# Revit family: NORFAC_WENT2000_med lysning
name_source: partatom
category: Windows
revit_build: Autodesk Revit 2018 (Build: 20170525_2315(x64)
units: mm (PartAtom-declared; Revit-internal decimal feet)

## family parameters
Always vertical = Yes
Cut with Voids When Loaded = No
Host = Wall
OmniClass Number = 23.30.20.00
OmniClass Title = Windows
Room Calculation Point = No
Shared = No

## types (1)
- TS-1-1
    Analytic Construction = <None>
    Case/Transom = RAL 9010
    Default Sill Height = 800 mm
    Eref energi balance = 4.223619
    Ew nord = -44.319266
    Ew syd = 45.80705
    Ew vest = -9.139952
    Ew øst = -9.139952
    Frame Area = 0.43 m²
    Frame Depth = 140 mm  [stored 0.459318 ft]
    Frame Width = 92 mm
    Frame/Mullion = Softwood, Lumber
    Glass Area = 1.08 m²
    Glass Height = 1319 mm
    Glass Material = BA - (o) - Glas
    Glass Width = 816 mm
    Height = 1503 mm
    Horiz Mullion 1 of 1 = No
    Horiz Mullion 1 of 2 = No
    Horiz Mullion 2 of 2 = No
    Joint = 10 mm  [stored 0.0328084 ft]
    Joint Material = Black Rubber
    LT value = 0
    Left Hinging = Yes
    Lysning = <By Category>
    Manual Height = 1523 mm
    Manual Width = 1020 mm
    Placement In Wall = 0 mm  [stored 0 ft]
    Psi Glass = 0.04
    Right Hinging = No
    Rough Height = 1523 mm
    Rough Width = 1020 mm
    Top Hinging = No
    U value = 0.809317
    U value Frame = 0.71
    U value Glass = 0.69
    Ventil mål mm = 689.5
    Ventilations luftmængde 10Pa, m3/t = 23.6
    Ventilations luftsmængde 4Pa, m3/t = 14.9
    Ventilations luftsmængde 8Pa, m3/t = 20.9
    Vinkel fra Nord = 180.00°
    Wall Closure = By host
    Width = 1000 mm  [stored 3.28084 ft]
    Window Area = 1.5 m²
    g value = 0.55
    gw = 0.393857

note: [stored X ft] marks values corroborated as IEEE doubles in the binary element streams (Revit-internal decimal feet)

## geometry (parser evidence)
native form markers: Sweep x14
no freeform markers — native parametric forms only
